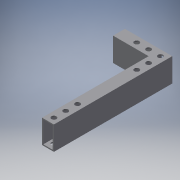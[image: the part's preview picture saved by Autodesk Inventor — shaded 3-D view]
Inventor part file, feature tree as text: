
AUTODESK INVENTOR PART (.ipt)
format: ipt  version: 2018 (Build 220112000, 112)  size: 181,248 bytes
history: native  units: in
note: dims shown in document units (in); Inventor stores cm internally (conversion verified against a paired STEP export)
features: extrude x5, sketch x5
ambient origin geometry x8: Origin, YZ Plane, XZ Plane, XY Plane, X Axis, Y Axis, Z Axis, Center Point
bodies: Body1 (feature_tree)
feature tree (10):
  extrude  "Extrusion12"  Depth=2.0in
  extrude  "Extrusion13"  Depth=0.1in
  extrude  "Extrusion14"  Depth=0.1in
  extrude  "Extrusion16"  Depth=1.0in
  extrude  "Extrusion17"  Depth=0.1in
  sketch  "Sketch15"  dims[d46=1.0in d47=2.0in]
  sketch  "Sketch16"  dims[d48=0.1in d49=0.1in]
  sketch  "Sketch17"  dims[d50=0.1in d51=0.1in]
  sketch  "Sketch20"  dims[d52=3.0in d53=0.0in d54=1.0in]
  sketch  "Sketch21"  dims[d55=2.0in d56=0.1in d57=0.1in d58=0.1in d59=0.1in d60=10.0in d61=0.0in d62=0.1in d63=0.0in d71=0.5in d72=0.5in d73=0.5in d74=0.4167in d75=0.4167in d76=0.4167in d77=0.5in d78=0.5in d79=0.4167in d80=0.4167in d81=0.5in d82=1.0in d83=1.0in d84=1.0in d85=1.0in d86=3.0in d87=0.0in d88=0.4167in d89=0.4167in d90=0.4167in d91=1.0in d92=1.0in d93=0.5in d94=0.5in d95=0.5in d96=0.5in d97=3.0in d98=0.0in]
